FCSTD DOCUMENT  (FreeCAD 0.20R29603 (Git))
Label: pointe_de_centrage_rouleau_aluminium
License: All rights reserved
LicenseURL: http://en.wikipedia.org/wiki/All_rights_reserved
objects: Sketcher::SketchObject×3, PartDesign::Body×1
note: 4 computed .brp shape members not serialized (recipe doc carries the construction recipe); baked Part::Feature solids carry a one-line shape summary decoded from their .brp

FEATURE [Sketcher::SketchObject] Sketch
  FullyConstrained = true
  MapMode = 5
  Support = -> [XY_Plane]
  sketch-geometry (13):
    g0: LineSegment StartX=-25 StartY=25 StartZ=0 EndX=-25 EndY=-25 EndZ=0
    g1: LineSegment StartX=-25 StartY=-25 StartZ=0 EndX=25 EndY=-25 EndZ=0
    g2: LineSegment StartX=5.3033 StartY=-5.3033 StartZ=0 EndX=-4.54505 EndY=-15.1517 EndZ=0
    g3: LineSegment StartX=-4.54505 StartY=-15.1517 StartZ=0 EndX=-15.1517 EndY=-4.54505 EndZ=0
    g4: LineSegment StartX=-15.1517 StartY=-4.54505 StartZ=0 EndX=-5.3033 EndY=5.3033 EndZ=0
    g5: LineSegment StartX=25 StartY=-25 StartZ=0 EndX=-25 EndY=25 EndZ=0
    g6: LineSegment StartX=-25 StartY=25 StartZ=0 EndX=14.3934 EndY=25 EndZ=0
    g7: LineSegment StartX=14.3934 StartY=25 StartZ=0 EndX=4.54505 EndY=15.1517 EndZ=0
    g8: LineSegment StartX=4.54505 StartY=15.1517 StartZ=0 EndX=15.1517 EndY=4.54505 EndZ=0
    g9: LineSegment StartX=15.1517 StartY=4.54505 StartZ=0 EndX=25 EndY=14.3934 EndZ=0
    g10: LineSegment StartX=25 StartY=14.3934 StartZ=0 EndX=25 EndY=-25 EndZ=0
    g11: LineSegment StartX=15.1517 StartY=4.54505 StartZ=0 EndX=5.3033 EndY=-5.3033 EndZ=0
    g12: LineSegment StartX=-15.1517 StartY=-4.54505 StartZ=0 EndX=-25 EndY=-14.3934 EndZ=0
  constraints (37):
    c: Vertical(g0)
    c: Coincident(g0,g1)
    c: Horizontal(g1)
    c: Coincident(g2,g3)
    c: Coincident(g3,g4)
    c: Equal(g0,g1)
    c: Perpendicular(g3,g4)
    c: Perpendicular(g2,g3)
    c: Coincident(g5,g6)
    c: Horizontal(g6)
    c: Coincident(g6,g7)
    c: Coincident(g7,g8)
    c: Coincident(g8,g9)
    c: Coincident(g9,g10)
    c: Coincident(g10,g5)
    c: Vertical(g10)
    c: Equal(g10,g6)
    c: Perpendicular(g8,g7)
    c: Perpendicular(g9,g8)
    c: Angle(g9,g10) = 0.785398
    c: Equal(g8,g3)
    c: Coincident(g11,g8)
    c: PointOnObject(g11,g5)
    c: Parallel(g11,g9)
    c: Equal(g11,g2)
    c: Coincident(g5,g0)
    c: Coincident(g1,g5)
    c: PointOnObject(g4,g5)
    c: Coincident(g2,g11)
    c: Parallel(g3,g8)
    c: Coincident(g12,g3)
    c: PointOnObject(g12,g0)
    c: Parallel(g4,g12)
    c: Equal(g12,g11)
    c: Symmetric(g4,g2,g-1)
    c: Distance(g3) = 15
    c: DistanceX(g1,g1) = 50
FEATURE [Sketcher::SketchObject] Sketch001
  FullyConstrained = true
  MapMode = 5
  Support = -> [XY_Plane]
  sketch-geometry (1):
    g0: Circle CenterX=0 CenterY=0 CenterZ=0 NormalX=0 NormalY=0 NormalZ=1 AngleXU=0 Radius=20
  constraints (2):
    c: Coincident(g0,g-1)
    c: Radius(g0) = 20
FEATURE [Sketcher::SketchObject] Sketch002
  FullyConstrained = true
  MapMode = 5
  Support = -> [XY_Plane]
  sketch-geometry (1):
    g0: Circle CenterX=0 CenterY=0 CenterZ=0 NormalX=0 NormalY=0 NormalZ=1 AngleXU=0 Radius=30
  constraints (2):
    c: Coincident(g0,g-1)
    c: Radius(g0) = 30
FEATURE [PartDesign::Body] Body
  Group = -> [Sketch,Sketch001,Sketch002]
  Origin = -> Origin
